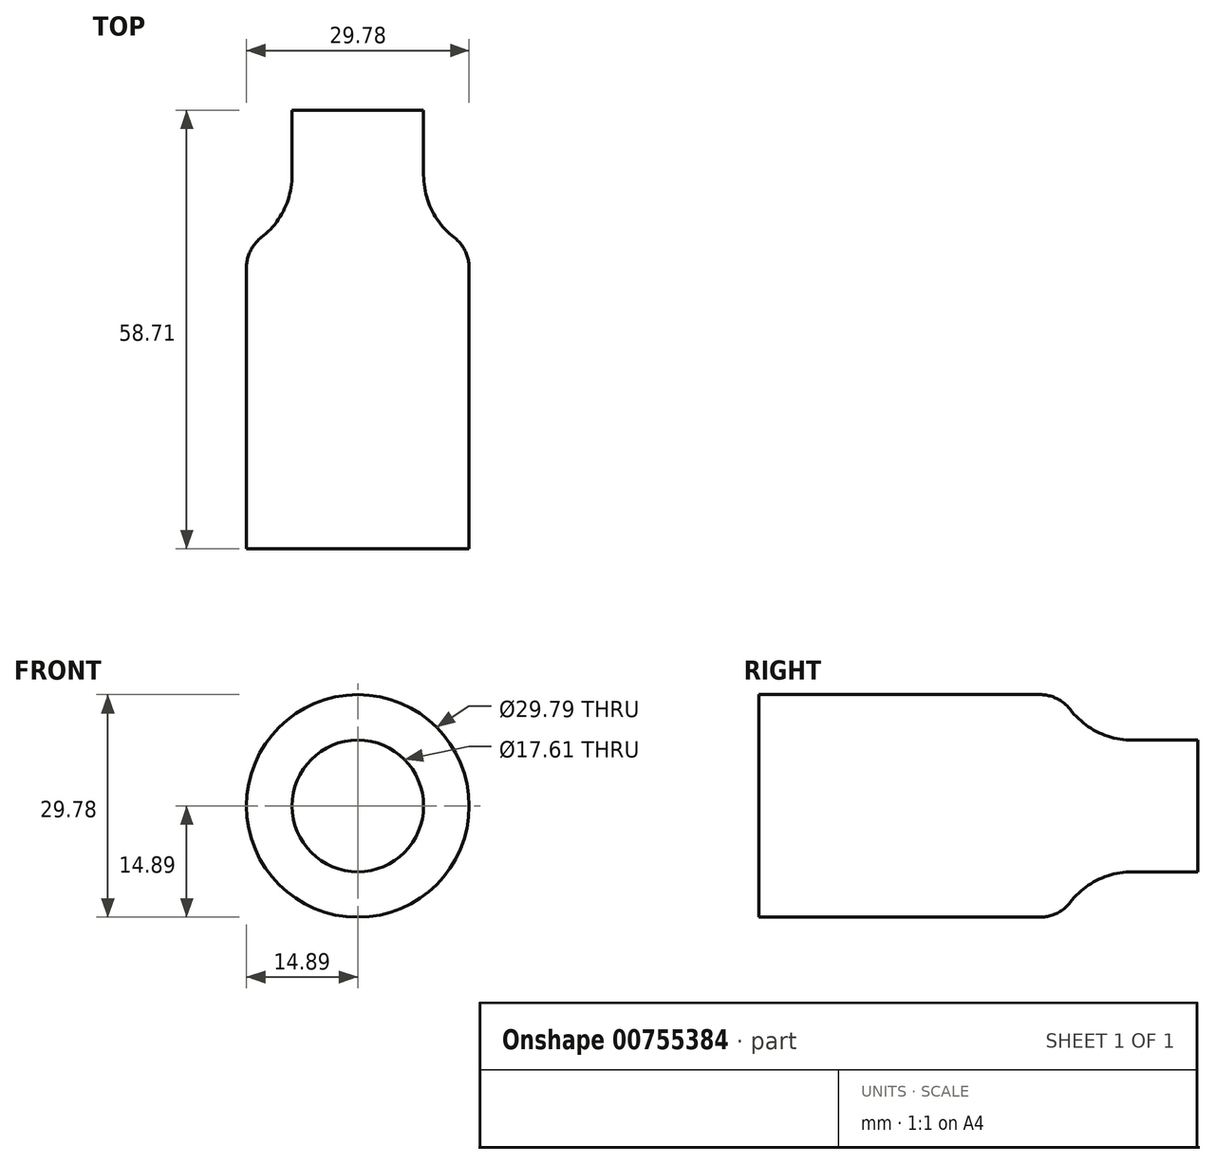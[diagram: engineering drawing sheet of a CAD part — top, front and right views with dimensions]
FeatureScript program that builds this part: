
annotation { "Feature Type Name" : "Feature", "Feature Type Description" : "" }
export const myFeature = defineFeature(function(context is Context, id is Id, definition is map)
    precondition{}
    {
        {
            var Q0;
            Q0=qCreatedBy(makeId("Right.planeOp"),FACE);
            var sketch = newSketch(context, id + "F0", { "sketchPlane" : qUnion([Q0])});
            skLineSegment(sketch, "E0", {"start": v(-54.69, 14.9) * mm, "end": v(-14.24, 14.9) * mm});
            skLineSegment(sketch, "E1", {"start": v(-4.67, 8.8) * mm, "end": v(4.02, 8.8) * mm});
            skArc(sketch, "E2", {"start": v(-4.67, 8.8) * mm, "mid": v(-10.34, 10.46) * mm, "end": v(-14.24, 14.9) * mm});
            skLineSegment(sketch, "E3", {"start": v(4.02, 8.8) * mm, "end": v(4.02, 0) * mm});
            skLineSegment(sketch, "E4", {"start": v(-54.69, 14.9) * mm, "end": v(-54.69, 0) * mm});
            skSolve(sketch);
        }
        {
            var Q0;
            Q0=qCreatedBy(makeId("Right.planeOp"),FACE);
            var sketch = newSketch(context, id + "F1", { "sketchPlane" : qUnion([Q0])});
            skLineSegment(sketch, "E5", {"start": v(-54.11, 0) * mm, "end": v(4, 0) * mm});
            skSolve(sketch);
        }
        {
            var Q0;
            Q0=sQuery(id+"F0.wireOp",EDGE,"E0");
            var Q1;
            Q1=sQuery(id+"F0.wireOp",EDGE,"E2");
            var Q2;
            Q2=sQuery(id+"F0.wireOp",EDGE,"E1");
            var Q3;
            Q3=sQuery(id+"F1.wireOp",EDGE,"E5");
            revolve(context, id + "F2", {"bodyType" : ToolBodyType.SURFACE, "surfaceOperationType" : NewSurfaceOperationType.NEW, "surfaceEntities" : qUnion([Q0, Q1, Q2]), "axis" : qUnion([Q3]), "revolveType" : RevolveType.FULL});
        }
        {
            var Q0;
            Q0=makeQuery(id+"F2.opRevolve","SWEPT_FACE",FACE,{"disambiguationData":[OSD([sQuery(id+"F0.wireOp",EDGE,"E0")])]});
            var Q1;
            Q1=makeQuery(id+"F2.opRevolve","SWEPT_FACE",FACE,{"disambiguationData":[OSD([sQuery(id+"F0.wireOp",EDGE,"E1")])]});
            fillet(context, id + "F3", {"entities" : qUnion([Q0, Q1]), "radius" : 5.08 * mm, "tangentPropagation" : true, "allowEdgeOverflow" : false});
        }
    });
